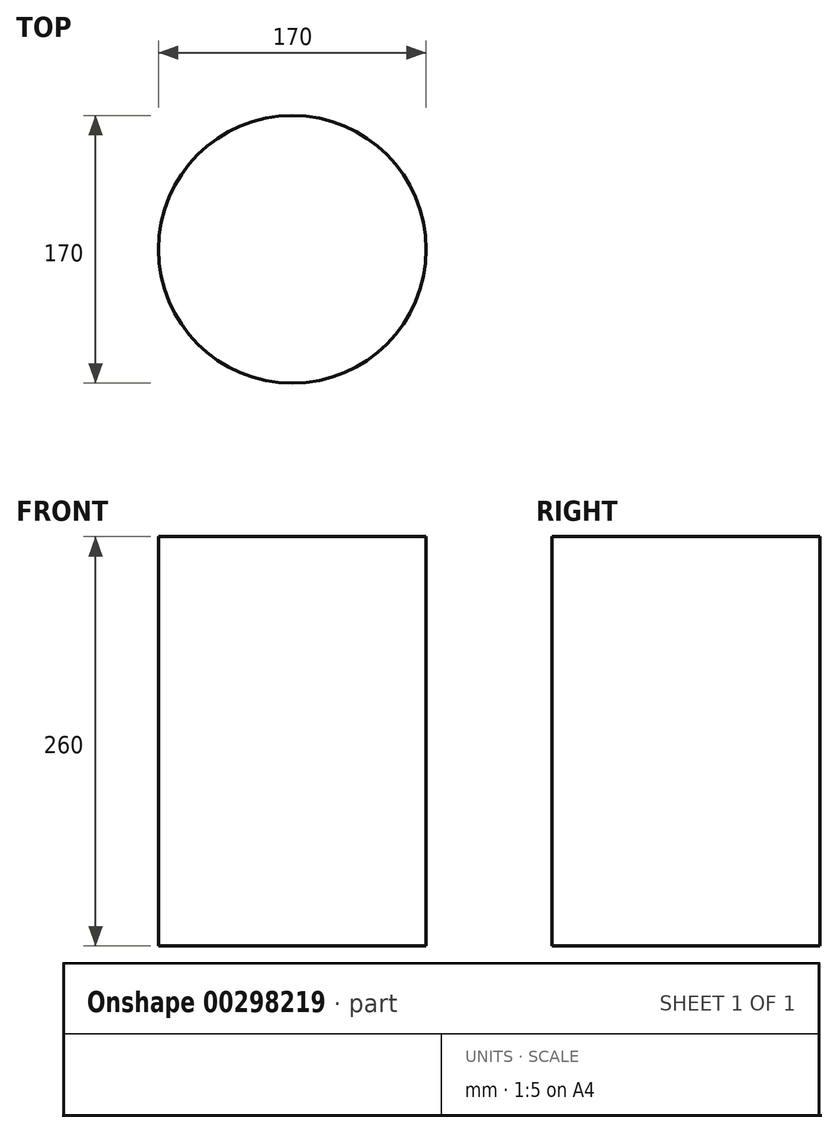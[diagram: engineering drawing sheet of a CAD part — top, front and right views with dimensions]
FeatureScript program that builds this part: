
annotation { "Feature Type Name" : "Feature", "Feature Type Description" : "" }
export const myFeature = defineFeature(function(context is Context, id is Id, definition is map)
    precondition{}
    {
        {
            var Q0;
            Q0=qCreatedBy(makeId("Top.planeOp"),FACE);
            var sketch = newSketch(context, id + "F0", { "sketchPlane" : qUnion([Q0])});
            skCircle(sketch, "E0", {"center": v(0, 0) * mm, "radius": 85 * mm});
            skSolve(sketch);
        }
        {
            var Q0;
            Q0=makeQuery(id+"F0.imprint","IMPRINT",FACE,{"disambiguationData":[TD([[makeQuery(id+"F0.imprint","IMPRINT",EDGE,{"derivedFrom":sQuery(id+"F0.wireOp",EDGE,"E0")}),1.0]])]});
            extrude(context, id + "F1", {"entities" : qUnion([Q0]), "depth" : 260 * mm});
        }
    });
